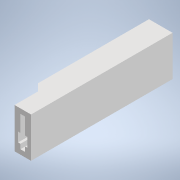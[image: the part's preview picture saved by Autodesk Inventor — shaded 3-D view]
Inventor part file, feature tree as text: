
AUTODESK INVENTOR PART (.ipt)
format: ipt  version: 2020 (Build 240168000, 168)  size: 155,136 bytes
history: native  units: mm
features: other x3, extrude x2, sketch x2, chamfer x1, thicken_offset x1, reference x1, projected_geometry x1
ambient origin geometry x8: Origin, YZ Plane, XZ Plane, XY Plane, X Axis, Y Axis, Z Axis, Center Point
bodies: Solid1 (feature_tree)
feature tree (11):
  extrude  "Extrusion1"  Depth=13.0mm
  extrude  "Extrusion2"  Depth=4.0mm
  chamfer  "Chamfer1"  Distance=2.0mm
  thicken_offset  "Thicken1"
  sketch  "Sketch1"  dims[d0=2.0mm d1=13.0mm]
  reference  "Reference1"
  sketch  "Sketch2"  dims[d2=4.0mm d3=4.0mm d4=2.0mm d5=17.0mm d6=1.5mm d7=2.0mm d8=2.0mm d9=50.0mm d10=0.0mm d11=3.0mm d12=1.0mm d13=1.0mm d14=10.0mm d15=0.0mm d16=3.0mm d17=2.0mm d18=45.0deg d19=0.2mm d20=0.2mm]
  projected_geometry  "Projected Loop1"
  parser-record x1  (decoder bookkeeping rows leaked as tree rows — omitted from the tree; the rows remain in map.json)
  other  "motorized2.iam"
  other  "servo_bracket:1"
note: 1 file-system path scrubbed to <path> (originals preserved in map.json)
